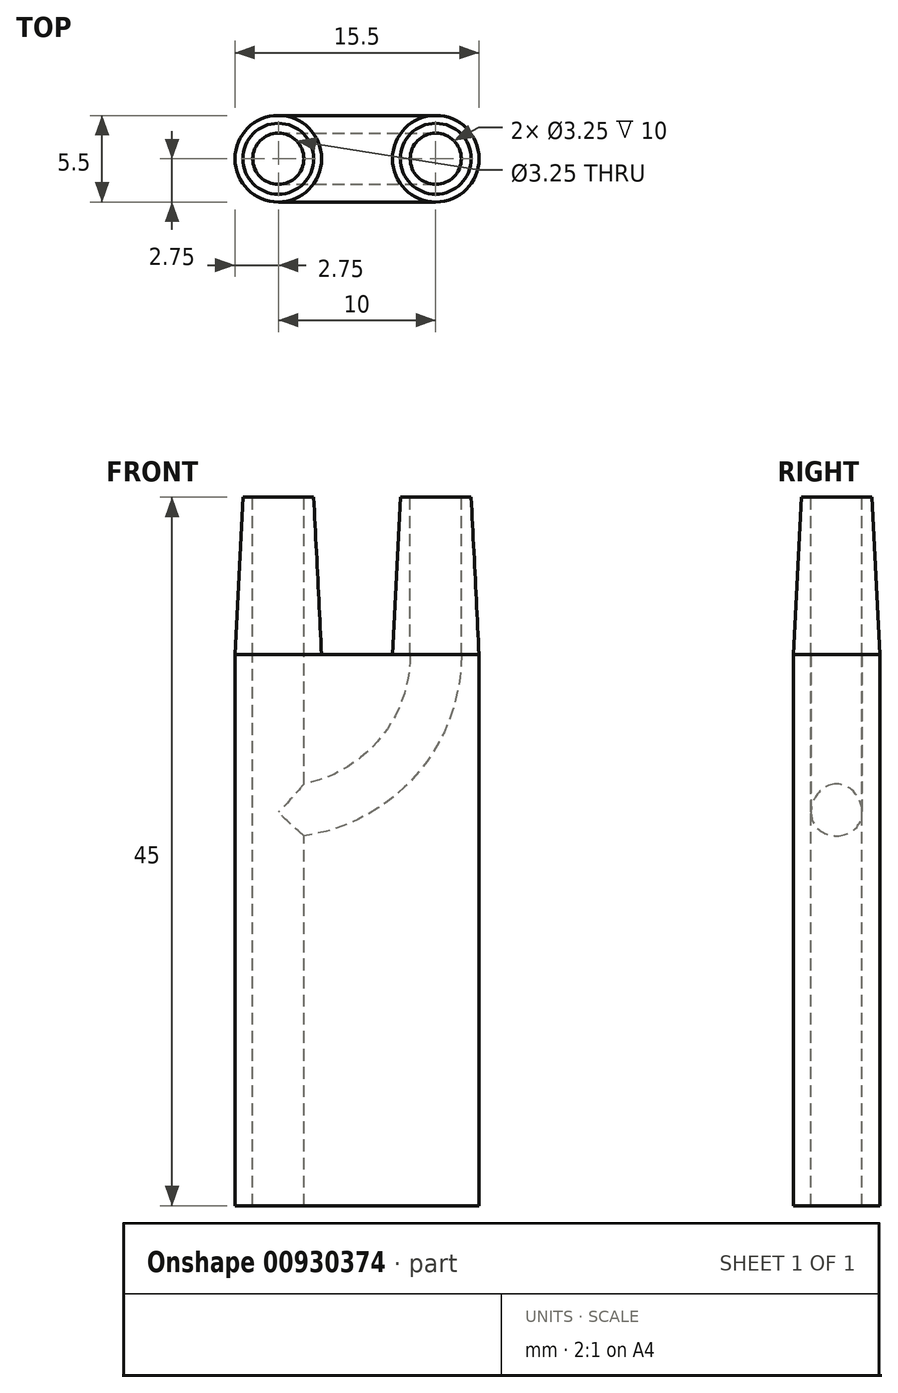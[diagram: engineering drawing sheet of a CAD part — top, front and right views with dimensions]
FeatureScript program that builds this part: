
annotation { "Feature Type Name" : "Feature", "Feature Type Description" : "" }
export const myFeature = defineFeature(function(context is Context, id is Id, definition is map)
    precondition{}
    {
        {
            var Q0;
            Q0=qCreatedBy(makeId("Front.planeOp"),FACE);
            var sketch = newSketch(context, id + "F0", { "sketchPlane" : qUnion([Q0])});
            skLineSegment(sketch, "E0", {"start": v(0, 0) * mm, "end": v(2.75, 0) * mm});
            skLineSegment(sketch, "E1", {"start": v(2.75, 0) * mm, "end": v(2.25, 10) * mm});
            skLineSegment(sketch, "E2", {"start": v(2.25, 10) * mm, "end": v(0, 10) * mm});
            skLineSegment(sketch, "E3", {"start": v(0, 10) * mm, "end": v(0, 0) * mm});
            skSolve(sketch);
        }
        {
            var Q0;
            Q0=makeQuery(id+"F0.imprint","IMPRINT",FACE,{"disambiguationData":[TD([[makeQuery(id+"F0.imprint","IMPRINT",EDGE,{"derivedFrom":sQuery(id+"F0.wireOp",EDGE,"E0")}),1.0]])]});
            var Q1;
            Q1=sQuery(id+"F0.wireOp",EDGE,"E3");
            revolve(context, id + "F1", {"surfaceOperationType" : NewSurfaceOperationType.NEW, "entities" : qUnion([Q0]), "axis" : qUnion([Q1]), "revolveType" : RevolveType.FULL});
        }
        {
            var Q0;
            Q0=makeQuery(id+"F1.opRevolve","SWEPT_FACE",FACE,{"disambiguationData":[OSD([sQuery(id+"F0.wireOp",EDGE,"E2")])]});
            var sketch = newSketch(context, id + "F2", { "sketchPlane" : qUnion([Q0])});
            skPoint(sketch, "E4", {"position": v(0, 0) * mm});
            skSolve(sketch);
        }
        {
            var Q0;
            Q0=sQuery(id+"F2.wireOp",VERTEX,"E4");
            var Q1;
            Q1=makeQuery(id+"F1.opRevolve","SWEPT_BODY",BODY,{"disambiguationData":[OSD([sQuery(id+"F0.wireOp",EDGE,"E0"),sQuery(id+"F0.wireOp",EDGE,"E1"),sQuery(id+"F0.wireOp",EDGE,"E2"),sQuery(id+"F0.wireOp",EDGE,"E3")])]});
            hole(context, id + "F3", {"style" : HoleStyle.SIMPLE, "endStyle" : HoleEndStyle.THROUGH, "holeDiameter" : 3.25 * mm, "majorDiameter" : 5 * mm, "isTappedThrough" : true, "tappedDepth" : 12 * mm, "tapClearance" : 3, "locations" : qUnion([Q0]), "scope" : qUnion([Q1])});
        }
        {
            var Q0;
            Q0=makeQuery(id+"F1.opRevolve","SWEPT_BODY",BODY,{"disambiguationData":[OSD([sQuery(id+"F0.wireOp",EDGE,"E0"),sQuery(id+"F0.wireOp",EDGE,"E1"),sQuery(id+"F0.wireOp",EDGE,"E2"),sQuery(id+"F0.wireOp",EDGE,"E3")])]});
            transform(context, id + "F4", {"entities" : qUnion([Q0]), "transformType" : TransformType.TRANSLATION_3D, "dx" : 10 * mm, "dy" : 0 * mm, "dz" : 0 * mm, "makeCopy" : true});
        }
        {
            var Q0;
            Q0=qCreatedBy(makeId("Front.planeOp"),FACE);
            var sketch = newSketch(context, id + "F5", { "sketchPlane" : qUnion([Q0])});
            skArc(sketch, "E5", {"start": v(10, 0) * mm, "mid": v(7.07, -7.07) * mm, "end": v(0, -10) * mm});
            skSolve(sketch);
        }
        {
            var Q0;
            Q0=makeQuery(id+"F4.opPattern","COPY",FACE,{"derivedFrom":makeQuery(id+"F1.opRevolve","SWEPT_FACE",FACE,{"disambiguationData":[OSD([sQuery(id+"F0.wireOp",EDGE,"E0")])]}),"instanceName":"1"});
            var sketch = newSketch(context, id + "F6", { "sketchPlane" : qUnion([Q0])});
            skCircle(sketch, "E6", {"center": v(10, 0) * mm, "radius": 1.63 * mm});
            skCircle(sketch, "E7", {"center": v(0, 0) * mm, "radius": 1.63 * mm});
            skSolve(sketch);
        }
        {
            var Q0;
            Q0=makeQuery(id+"F6.imprint","IMPRINT",FACE,{"disambiguationData":[TD([[makeQuery(id+"F6.imprint","IMPRINT",EDGE,{"derivedFrom":sQuery(id+"F6.wireOp",EDGE,"E6")}),1.0]])]});
            var Q1;
            Q1=sQuery(id+"F5.wireOp",EDGE,"E5");
            sweep(context, id + "F7", {"profiles" : qUnion([Q0]), "path" : qUnion([Q1])});
        }
        {
            var Q0;
            Q0=makeQuery(id+"F1.opRevolve","SWEPT_FACE",FACE,{"disambiguationData":[OSD([sQuery(id+"F0.wireOp",EDGE,"E0")])]});
            var sketch = newSketch(context, id + "F8", { "sketchPlane" : qUnion([Q0])});
            skCircle(sketch, "E8", {"center": v(0, 0) * mm, "radius": 1.63 * mm});
            skSolve(sketch);
        }
        {
            var Q0;
            Q0=makeQuery(id+"F8.imprint","IMPRINT",FACE,{"disambiguationData":[TD([[makeQuery(id+"F8.imprint","IMPRINT",EDGE,{"derivedFrom":sQuery(id+"F8.wireOp",EDGE,"E8")}),1.0]])]});
            extrude(context, id + "F9", {"entities" : qUnion([Q0]), "operationType" : NewBodyOperationType.ADD, "depth" : 15 * mm, "offsetDistance" : 25 * mm});
        }
        {
            var Q0;
            Q0=qCreatedBy(makeId("Top.planeOp"),FACE);
            var sketch = newSketch(context, id + "F10", { "sketchPlane" : qUnion([Q0])});
            skArc(sketch, "E9", {"start": v(0, 2.75) * mm, "mid": v(-2.75, 0) * mm, "end": v(0, -2.75) * mm});
            skArc(sketch, "E10", {"start": v(10, -2.75) * mm, "mid": v(12.75, 0) * mm, "end": v(10, 2.75) * mm});
            skLineSegment(sketch, "E11.bottom", {"start": v(0, 2.75) * mm, "end": v(10, 2.75) * mm});
            skLineSegment(sketch, "E11.top", {"start": v(0, -2.75) * mm, "end": v(10, -2.75) * mm});
            skSolve(sketch);
        }
        {
            var Q0;
            Q0=makeQuery(id+"F10.imprint","IMPRINT",FACE,{"disambiguationData":[TD([[makeQuery(id+"F10.imprint","IMPRINT",EDGE,{"derivedFrom":sQuery(id+"F10.wireOp",EDGE,"E9")}),1.0]])]});
            extrude(context, id + "F11", {"entities" : qUnion([Q0]), "oppositeDirection" : true, "depth" : 15 * mm, "offsetDistance" : 25 * mm});
        }
        {
            var Q0;
            Q0=makeQuery(id+"F7.opSweep","SWEPT_BODY",BODY,{"disambiguationData":[OSD([sQuery(id+"F5.wireOp",EDGE,"E5"),sQuery(id+"F6.wireOp",EDGE,"E6")])]});
            var Q1;
            Q1=makeQuery(id+"F11.opExtrude","SWEPT_BODY",BODY,{"disambiguationData":[OSD([sQuery(id+"F10.wireOp",EDGE,"E9"),sQuery(id+"F10.wireOp",EDGE,"E10"),sQuery(id+"F10.wireOp",EDGE,"E11.bottom"),sQuery(id+"F10.wireOp",EDGE,"E11.top")])]});
            booleanBodies(context, id + "F12", {"operationType" : BooleanOperationType.SUBTRACTION, "tools" : qUnion([Q0]), "targets" : qUnion([Q1])});
        }
        {
            var Q0;
            Q0=makeQuery(id+"F11.opExtrude","CAP_FACE",FACE,{"disambiguationData":[OSD([sQuery(id+"F10.wireOp",EDGE,"E9"),sQuery(id+"F10.wireOp",EDGE,"E10"),sQuery(id+"F10.wireOp",EDGE,"E11.bottom"),sQuery(id+"F10.wireOp",EDGE,"E11.top")])],"isStart":false});
            extrude(context, id + "F13", {"entities" : qUnion([Q0]), "operationType" : NewBodyOperationType.ADD, "depth" : 20 * mm, "offsetDistance" : 25 * mm});
        }
    });
